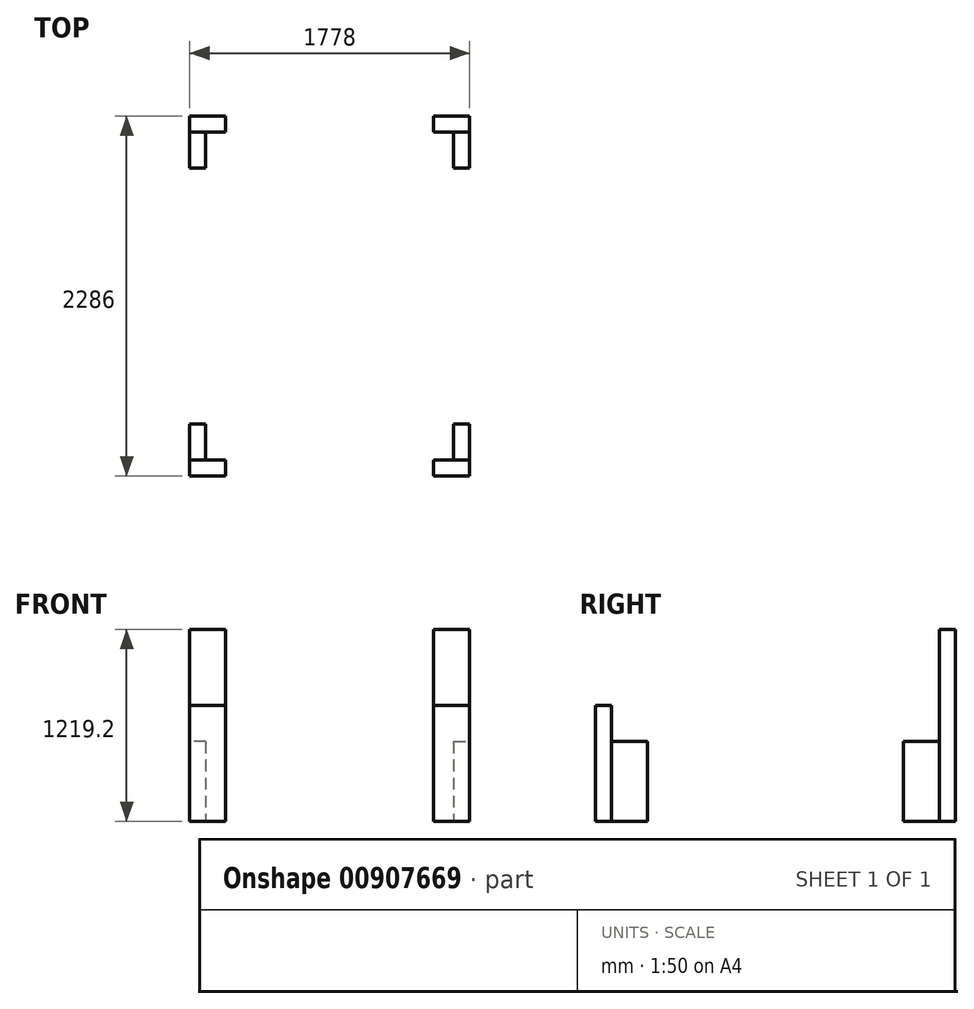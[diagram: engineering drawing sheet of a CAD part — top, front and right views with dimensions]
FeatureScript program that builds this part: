
annotation { "Feature Type Name" : "Feature", "Feature Type Description" : "" }
export const myFeature = defineFeature(function(context is Context, id is Id, definition is map)
    precondition{}
    {
        {
            var Q0;
            Q0=qCreatedBy(makeId("Top.planeOp"),FACE);
            var sketch = newSketch(context, id + "F0", { "sketchPlane" : qUnion([Q0])});
            skLineSegment(sketch, "E0.bottom", {"start": v(-127, 25.43) * mm, "end": v(101.6, 25.43) * mm});
            skLineSegment(sketch, "E0.top", {"start": v(-127, 127.03) * mm, "end": v(101.6, 127.03) * mm});
            skLineSegment(sketch, "E0.left", {"start": v(-127, 25.43) * mm, "end": v(-127, 127.03) * mm});
            skLineSegment(sketch, "E0.right", {"start": v(101.6, 25.43) * mm, "end": v(101.6, 127.03) * mm});
            skPoint(sketch, "E0.middle", {"position": v(-12.7, 76.23) * mm});
            skLineSegment(sketch, "E1.bottom", {"start": v(101.6, 25.43) * mm, "end": v(0, 25.43) * mm});
            skLineSegment(sketch, "E1.top", {"start": v(101.6, -203.17) * mm, "end": v(0, -203.17) * mm});
            skLineSegment(sketch, "E1.left", {"start": v(101.6, 25.43) * mm, "end": v(101.6, -203.17) * mm});
            skLineSegment(sketch, "E1.right", {"start": v(0, 25.43) * mm, "end": v(0, -203.17) * mm});
            skLineSegment(sketch, "E2.bottom", {"start": v(101.6, -1828.77) * mm, "end": v(0, -1828.77) * mm});
            skLineSegment(sketch, "E2.top", {"start": v(101.6, -2057.37) * mm, "end": v(0, -2057.37) * mm});
            skLineSegment(sketch, "E2.left", {"start": v(101.6, -1828.77) * mm, "end": v(101.6, -2057.37) * mm});
            skLineSegment(sketch, "E2.right", {"start": v(0, -1828.77) * mm, "end": v(0, -2057.37) * mm});
            skLineSegment(sketch, "E3.bottom", {"start": v(101.6, -2057.37) * mm, "end": v(-127, -2057.37) * mm});
            skLineSegment(sketch, "E3.top", {"start": v(101.6, -2158.97) * mm, "end": v(-127, -2158.97) * mm});
            skLineSegment(sketch, "E3.left", {"start": v(101.6, -2057.37) * mm, "end": v(101.6, -2158.97) * mm});
            skLineSegment(sketch, "E3.right", {"start": v(-127, -2057.37) * mm, "end": v(-127, -2158.97) * mm});
            skLineSegment(sketch, "E4.bottom", {"start": v(-1447.8, 25.43) * mm, "end": v(-1676.4, 25.43) * mm});
            skLineSegment(sketch, "E4.top", {"start": v(-1447.8, 127.03) * mm, "end": v(-1676.4, 127.03) * mm});
            skLineSegment(sketch, "E4.left", {"start": v(-1447.8, 25.43) * mm, "end": v(-1447.8, 127.03) * mm});
            skLineSegment(sketch, "E4.right", {"start": v(-1676.4, 25.43) * mm, "end": v(-1676.4, 127.03) * mm});
            skLineSegment(sketch, "E5.bottom", {"start": v(-1676.4, 25.43) * mm, "end": v(-1574.8, 25.43) * mm});
            skLineSegment(sketch, "E5.top", {"start": v(-1676.4, -203.17) * mm, "end": v(-1574.8, -203.17) * mm});
            skLineSegment(sketch, "E5.left", {"start": v(-1676.4, 25.43) * mm, "end": v(-1676.4, -203.17) * mm});
            skLineSegment(sketch, "E5.right", {"start": v(-1574.8, 25.43) * mm, "end": v(-1574.8, -203.17) * mm});
            skLineSegment(sketch, "E6.bottom", {"start": v(-1447.8, -2057.37) * mm, "end": v(-1676.4, -2057.37) * mm});
            skLineSegment(sketch, "E6.top", {"start": v(-1447.8, -2158.97) * mm, "end": v(-1676.4, -2158.97) * mm});
            skLineSegment(sketch, "E6.left", {"start": v(-1447.8, -2057.37) * mm, "end": v(-1447.8, -2158.97) * mm});
            skLineSegment(sketch, "E6.right", {"start": v(-1676.4, -2057.37) * mm, "end": v(-1676.4, -2158.97) * mm});
            skLineSegment(sketch, "E7.bottom", {"start": v(-1676.4, -2057.37) * mm, "end": v(-1574.8, -2057.37) * mm});
            skLineSegment(sketch, "E7.top", {"start": v(-1676.4, -1828.77) * mm, "end": v(-1574.8, -1828.77) * mm});
            skLineSegment(sketch, "E7.left", {"start": v(-1676.4, -2057.37) * mm, "end": v(-1676.4, -1828.77) * mm});
            skLineSegment(sketch, "E7.right", {"start": v(-1574.8, -2057.37) * mm, "end": v(-1574.8, -1828.77) * mm});
            skSolve(sketch);
        }
        {
            var Q0;
            Q0=makeQuery(id+"F0.imprint","IMPRINT",FACE,{"disambiguationData":[TD([[makeQuery(id+"F0.imprint","IMPRINT",EDGE,{"derivedFrom":sQuery(id+"F0.wireOp",EDGE,"E6.top")}),-1.0]])]});
            var Q1;
            Q1=makeQuery(id+"F0.imprint","IMPRINT",FACE,{"disambiguationData":[TD([[makeQuery(id+"F0.imprint","IMPRINT",EDGE,{"derivedFrom":sQuery(id+"F0.wireOp",EDGE,"E2.top")}),1.0]])]});
            extrude(context, id + "F1", {"entities" : qUnion([Q0, Q1]), "depth" : 736.6 * mm, "offsetDistance" : 25.4 * mm});
        }
        {
            var Q0;
            Q0=makeQuery(id+"F0.imprint","IMPRINT",FACE,{"disambiguationData":[TD([[makeQuery(id+"F0.imprint","IMPRINT",EDGE,{"derivedFrom":sQuery(id+"F0.wireOp",EDGE,"E4.top")}),1.0]])]});
            var Q1;
            Q1=makeQuery(id+"F0.imprint","IMPRINT",FACE,{"disambiguationData":[TD([[makeQuery(id+"F0.imprint","IMPRINT",EDGE,{"derivedFrom":sQuery(id+"F0.wireOp",EDGE,"E0.top")}),-1.0]])]});
            extrude(context, id + "F2", {"entities" : qUnion([Q0, Q1]), "depth" : 1219.2 * mm, "offsetDistance" : 25.4 * mm});
        }
        {
            var Q0;
            Q0=makeQuery(id+"F0.imprint","IMPRINT",FACE,{"disambiguationData":[TD([[makeQuery(id+"F0.imprint","IMPRINT",EDGE,{"derivedFrom":sQuery(id+"F0.wireOp",EDGE,"E5.top")}),1.0]])]});
            var Q1;
            Q1=makeQuery(id+"F0.imprint","IMPRINT",FACE,{"disambiguationData":[TD([[makeQuery(id+"F0.imprint","IMPRINT",EDGE,{"derivedFrom":sQuery(id+"F0.wireOp",EDGE,"E1.top")}),-1.0]])]});
            var Q2;
            Q2=makeQuery(id+"F0.imprint","IMPRINT",FACE,{"disambiguationData":[TD([[makeQuery(id+"F0.imprint","IMPRINT",EDGE,{"derivedFrom":sQuery(id+"F0.wireOp",EDGE,"E7.top")}),-1.0]])]});
            var Q3;
            Q3=makeQuery(id+"F0.imprint","IMPRINT",FACE,{"disambiguationData":[TD([[makeQuery(id+"F0.imprint","IMPRINT",EDGE,{"derivedFrom":sQuery(id+"F0.wireOp",EDGE,"E2.bottom")}),1.0]])]});
            extrude(context, id + "F3", {"entities" : qUnion([Q0, Q1, Q2, Q3]), "depth" : 508 * mm, "offsetDistance" : 25.4 * mm});
        }
    });
